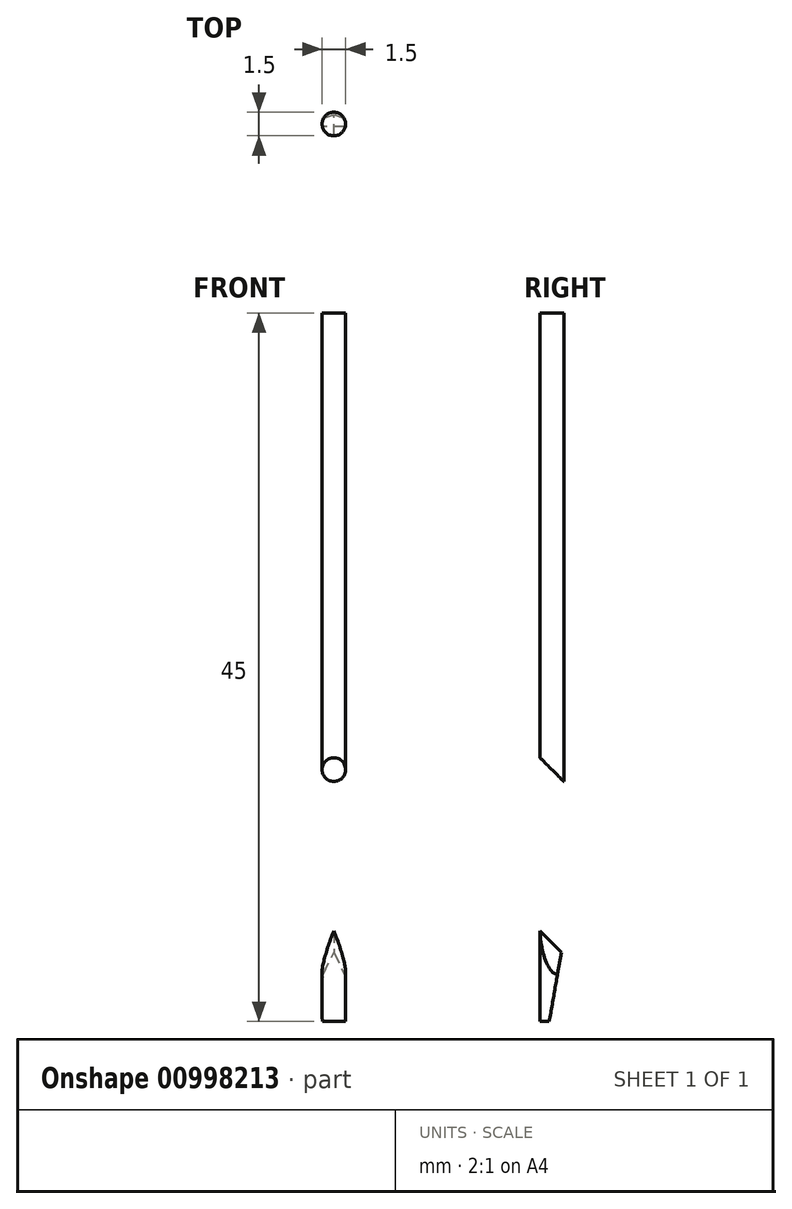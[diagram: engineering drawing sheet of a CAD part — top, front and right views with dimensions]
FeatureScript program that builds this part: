
annotation { "Feature Type Name" : "Feature", "Feature Type Description" : "" }
export const myFeature = defineFeature(function(context is Context, id is Id, definition is map)
    precondition{}
    {
        {
            var Q0;
            Q0=qCreatedBy(makeId("Top.planeOp"),FACE);
            var sketch = newSketch(context, id + "F0", { "sketchPlane" : qUnion([Q0])});
            skCircle(sketch, "E0", {"center": v(0, 0) * mm, "radius": 0.75 * mm});
            skLineSegment(sketch, "E1", {"start": v(0, 0) * mm, "end": v(12.04, 0) * mm, "construction": true});
            skSolve(sketch);
        }
        {
            var Q0;
            Q0 = qSketchRegion(id + "F0", true);
            extrude(context, id + "F1", {"entities" : qUnion([Q0]), "depth" : 40 * mm, "offsetDistance" : 25 * mm, "hasSecondDirection" : true, "secondDirectionOppositeDirection" : true, "secondDirectionDepth" : 5 * mm});
        }
        {
            var Q0;
            Q0=sQuery(id+"F0.wireOp",EDGE,"E1");
            var Q1;
            Q1=qCreatedBy(makeId("Top.planeOp"),FACE);
            cPlane(context, id + "F2", {"entities" : qUnion([Q0, Q1]), "cplaneType" : CPlaneType.LINE_ANGLE, "offset" : 25 * mm, "angle" : 45 * degree, "width" : 150 * mm, "height" : 150 * mm});
        }
        {
            var Q0;
            Q0=qCreatedBy(id+"F2.planeOp",FACE);
            var sketch = newSketch(context, id + "F3", { "sketchPlane" : qUnion([Q0])});
            skLineSegment(sketch, "E2", {"start": v(0, 0) * mm, "end": v(3.6, -6.23) * mm});
            skLineSegment(sketch, "E3", {"start": v(3.6, -6.23) * mm, "end": v(3.6, 7.77) * mm});
            skLineSegment(sketch, "E4", {"start": v(3.6, 7.77) * mm, "end": v(-3.6, 7.77) * mm});
            skLineSegment(sketch, "E5", {"start": v(-3.6, 7.77) * mm, "end": v(-3.6, -6.23) * mm});
            skLineSegment(sketch, "E6", {"start": v(-3.6, -6.23) * mm, "end": v(0, 0) * mm});
            skSolve(sketch);
        }
        {
            var Q0;
            Q0 = qSketchRegion(id + "F3", true);
            extrude(context, id + "F4", {"entities" : qUnion([Q0]), "operationType" : NewBodyOperationType.REMOVE, "endBound" : BoundingType.THROUGH_ALL, "oppositeDirection" : true, "depth" : 25 * mm, "offsetDistance" : 25 * mm, "hasSecondDirection" : true, "secondDirectionBound" : SecondDirectionBoundingType.THROUGH_ALL, "secondDirectionOppositeDirection" : false, "secondDirectionDepth" : 25 * mm});
        }
        {
            var Q0;
            Q0=qCreatedBy(id+"F2.planeOp",FACE);
            var Q1;
            Q1=sQuery(id+"F0.wireOp",EDGE,"E1");
            cPlane(context, id + "F5", {"entities" : qUnion([Q0, Q1]), "cplaneType" : CPlaneType.LINE_ANGLE, "offset" : 25 * mm, "angle" : 125 * degree, "width" : 150 * mm, "height" : 150 * mm});
        }
        {
            var Q0;
            Q0=qCreatedBy(id+"F5.planeOp",FACE);
            var sketch = newSketch(context, id + "F6", { "sketchPlane" : qUnion([Q0])});
            skLineSegment(sketch, "E7.bottom", {"start": v(3.08, -3.44) * mm, "end": v(-3.36, -3.44) * mm});
            skLineSegment(sketch, "E7.top", {"start": v(3.08, -0.7) * mm, "end": v(-3.36, -0.7) * mm});
            skLineSegment(sketch, "E7.left", {"start": v(3.08, -3.44) * mm, "end": v(3.08, -0.7) * mm});
            skLineSegment(sketch, "E7.right", {"start": v(-3.36, -3.44) * mm, "end": v(-3.36, -0.7) * mm});
            skSolve(sketch);
        }
        {
            var Q0;
            Q0 = qSketchRegion(id + "F6", true);
            extrude(context, id + "F7", {"entities" : qUnion([Q0]), "operationType" : NewBodyOperationType.REMOVE, "endBound" : BoundingType.THROUGH_ALL, "depth" : 25 * mm, "offsetDistance" : 25 * mm, "hasSecondDirection" : true, "secondDirectionBound" : SecondDirectionBoundingType.THROUGH_ALL, "secondDirectionOppositeDirection" : true, "secondDirectionDepth" : 25 * mm});
        }
    });
